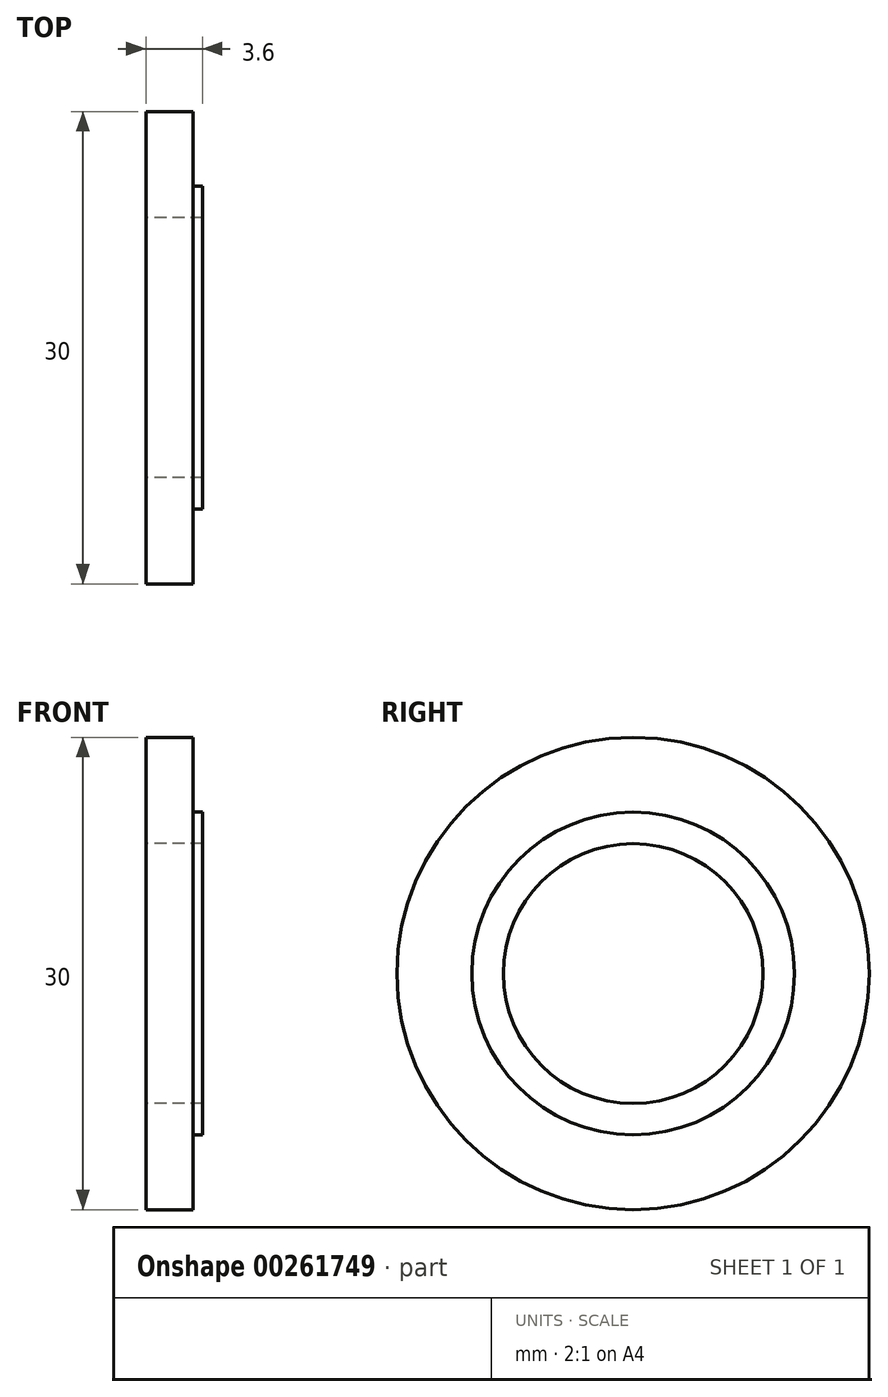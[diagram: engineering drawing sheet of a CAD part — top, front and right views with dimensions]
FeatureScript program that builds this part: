
annotation { "Feature Type Name" : "Feature", "Feature Type Description" : "" }
export const myFeature = defineFeature(function(context is Context, id is Id, definition is map)
    precondition{}
    {
        {
            var Q0;
            Q0=qCreatedBy(makeId("Front.planeOp"),FACE);
            var sketch = newSketch(context, id + "F0", { "sketchPlane" : qUnion([Q0])});
            skLineSegment(sketch, "E0", {"start": v(0.6, 8.25) * mm, "end": v(-3, 8.25) * mm});
            skLineSegment(sketch, "E1", {"start": v(-3, 8.25) * mm, "end": v(-3, 15) * mm});
            skLineSegment(sketch, "E2", {"start": v(-3, 15) * mm, "end": v(0, 15) * mm});
            skLineSegment(sketch, "E3", {"start": v(0, 15) * mm, "end": v(0, 10.25) * mm});
            skLineSegment(sketch, "E4", {"start": v(0, 10.25) * mm, "end": v(0.6, 10.25) * mm});
            skLineSegment(sketch, "E5", {"start": v(0.6, 10.25) * mm, "end": v(0.6, 8.25) * mm});
            skLineSegment(sketch, "E6", {"start": v(-41.36, 0) * mm, "end": v(47.7, 0) * mm, "construction": true});
            skSolve(sketch);
        }
        {
            var Q0;
            Q0=makeQuery(id+"F0.imprint","IMPRINT",FACE,{"disambiguationData":[TD([[makeQuery(id+"F0.imprint","IMPRINT",EDGE,{"derivedFrom":sQuery(id+"F0.wireOp",EDGE,"E0")}),-1.0]])]});
            var Q1;
            Q1=sQuery(id+"F0.wireOp",EDGE,"E6");
            revolve(context, id + "F1", {"entities" : qUnion([Q0]), "axis" : qUnion([Q1]), "revolveType" : RevolveType.FULL});
        }
    });
